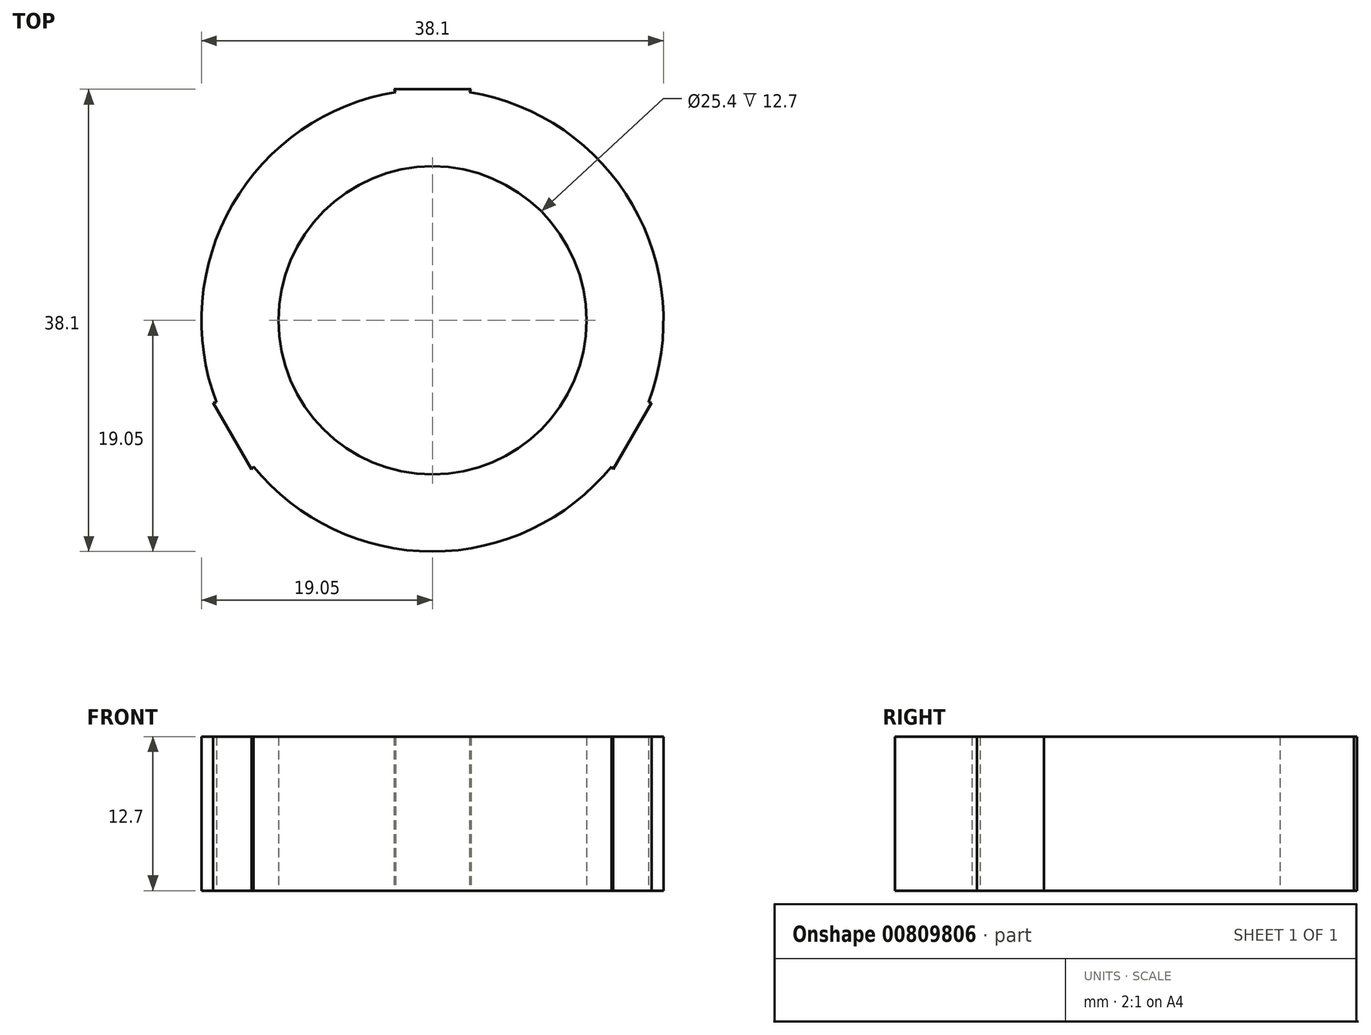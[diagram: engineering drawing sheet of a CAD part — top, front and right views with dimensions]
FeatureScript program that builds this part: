
annotation { "Feature Type Name" : "Feature", "Feature Type Description" : "" }
export const myFeature = defineFeature(function(context is Context, id is Id, definition is map)
    precondition{}
    {
        {
            var Q0;
            Q0=qCreatedBy(makeId("Top.planeOp"),FACE);
            var sketch = newSketch(context, id + "F0", { "sketchPlane" : qUnion([Q0])});
            skCircle(sketch, "E0", {"center": v(0, 0) * mm, "radius": 12.7 * mm});
            skCircle(sketch, "E1", {"center": v(0, 0) * mm, "radius": 19.05 * mm});
            skLineSegment(sketch, "E2", {"start": v(0, 19.05) * mm, "end": v(0, 12.7) * mm});
            skLineSegment(sketch, "E3", {"start": v(-16.5, -9.53) * mm, "end": v(-11, -6.35) * mm});
            skLineSegment(sketch, "E4", {"start": v(16.5, -9.53) * mm, "end": v(11, -6.35) * mm});
            skLineSegment(sketch, "E5", {"start": v(-16.5, -9.53) * mm, "end": v(-18.09, -6.78) * mm});
            skLineSegment(sketch, "E6", {"start": v(-16.5, -9.53) * mm, "end": v(-14.91, -12.27) * mm});
            skLineSegment(sketch, "E7", {"start": v(-14.91, -12.27) * mm, "end": v(-11, -6.35) * mm});
            skLineSegment(sketch, "E8", {"start": v(-11, -6.35) * mm, "end": v(-18.09, -6.78) * mm});
            skLineSegment(sketch, "E9", {"start": v(0, 19.05) * mm, "end": v(-3.18, 19.05) * mm});
            skLineSegment(sketch, "E10", {"start": v(0, 19.05) * mm, "end": v(3.18, 19.05) * mm});
            skLineSegment(sketch, "E11", {"start": v(-3.18, 19.05) * mm, "end": v(0, 12.7) * mm});
            skLineSegment(sketch, "E12", {"start": v(0, 12.7) * mm, "end": v(3.18, 19.05) * mm});
            skLineSegment(sketch, "E13", {"start": v(16.5, -9.53) * mm, "end": v(18.09, -6.78) * mm});
            skLineSegment(sketch, "E14", {"start": v(16.5, -9.53) * mm, "end": v(14.91, -12.27) * mm});
            skLineSegment(sketch, "E15", {"start": v(14.91, -12.27) * mm, "end": v(11, -6.35) * mm});
            skLineSegment(sketch, "E16", {"start": v(11, -6.35) * mm, "end": v(18.09, -6.78) * mm});
            skSolve(sketch);
        }
        {
            var Q0;
            Q0=qSketchRegion(id+"F0",true);
            extrude(context, id + "F1", {"entities" : qUnion([Q0]), "depth" : 12.7 * mm, "offsetDistance" : 25.4 * mm});
        }
    });
